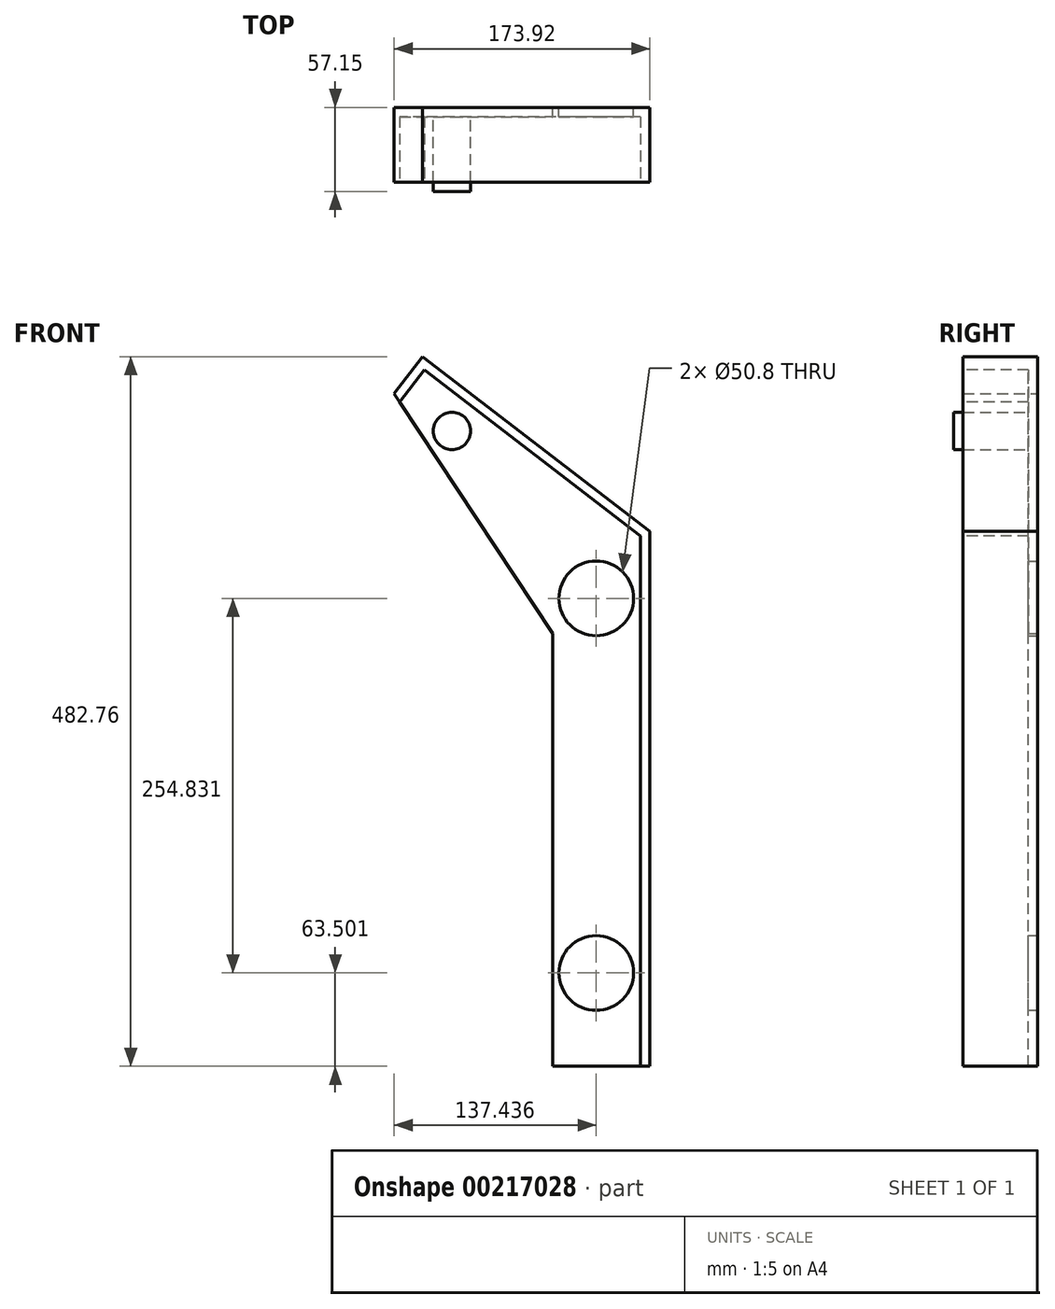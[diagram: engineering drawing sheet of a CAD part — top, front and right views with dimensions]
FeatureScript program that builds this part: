
annotation { "Feature Type Name" : "Feature", "Feature Type Description" : "" }
export const myFeature = defineFeature(function(context is Context, id is Id, definition is map)
    precondition{}
    {
        {
            var Q0;
            Q0=qCreatedBy(makeId("Front.planeOp"),FACE);
            var sketch = newSketch(context, id + "F0", { "sketchPlane" : qUnion([Q0])});
            skLineSegment(sketch, "E0.bottom", {"start": v(31, -269.09) * mm, "end": v(-35.03, -269.09) * mm});
            skLineSegment(sketch, "E0.left", {"start": v(31, -269.09) * mm, "end": v(31, 94.95) * mm});
            skLineSegment(sketch, "E0.right", {"start": v(-35.03, -269.09) * mm, "end": v(-35.03, 25.3) * mm});
            skPoint(sketch, "E0.middle", {"position": v(-5.47, 49.24) * mm});
            skLineSegment(sketch, "E1", {"start": v(31, 94.95) * mm, "end": v(-123.57, 213.67) * mm});
            skLineSegment(sketch, "E2", {"start": v(-123.57, 213.67) * mm, "end": v(-142.91, 188.5) * mm});
            skLineSegment(sketch, "E3", {"start": v(-142.91, 188.5) * mm, "end": v(-35.03, 25.3) * mm});
            skCircle(sketch, "E4", {"center": v(-5.47, 49.24) * mm, "radius": 25.4 * mm});
            skCircle(sketch, "E5", {"center": v(-5.47, -205.59) * mm, "radius": 25.4 * mm});
            skSolve(sketch);
        }
        {
            var Q0;
            Q0=makeQuery(id+"F0.imprint","IMPRINT",FACE,{"disambiguationData":[TD([[makeQuery(id+"F0.imprint","IMPRINT",EDGE,{"derivedFrom":sQuery(id+"F0.wireOp",EDGE,"E0.bottom")}),-1.0]])]});
            extrude(context, id + "F1", {"entities" : qUnion([Q0]), "depth" : 50.8 * mm});
        }
        {
            var Q0;
            Q0=makeQuery(id+"F1.opExtrude","CAP_FACE",FACE,{"disambiguationData":[OSD([sQuery(id+"F0.wireOp",EDGE,"E0.bottom"),sQuery(id+"F0.wireOp",EDGE,"E0.left"),sQuery(id+"F0.wireOp",EDGE,"E0.right"),sQuery(id+"F0.wireOp",EDGE,"E1"),sQuery(id+"F0.wireOp",EDGE,"E2"),sQuery(id+"F0.wireOp",EDGE,"E3"),sQuery(id+"F0.wireOp",EDGE,"E4"),sQuery(id+"F0.wireOp",EDGE,"E5")])],"isStart":false});
            var sketch = newSketch(context, id + "F2", { "sketchPlane" : qUnion([Q0])});
            skLineSegment(sketch, "E6.0", {"start": v(-122.4, 204.77) * mm, "end": v(-139.2, 182.89) * mm});
            skLineSegment(sketch, "E6.1", {"start": v(24.66, 91.82) * mm, "end": v(-122.4, 204.77) * mm});
            skLineSegment(sketch, "E6.2", {"start": v(24.66, -269.09) * mm, "end": v(24.66, 91.82) * mm});
            skSolve(sketch);
        }
        {
            var Q0;
            {var subQ3=sQuery(id+"F2.wireOp",EDGE,"E6.0");Q0=makeQuery(id+"F2.imprint","IMPRINT",FACE,{"disambiguationData":[TD([[makeQuery(id+"F2.imprint","IMPRINT",EDGE,{"derivedFrom":subQ3}),1.0]])]});}
            extrude(context, id + "F3", {"entities" : qUnion([Q0]), "operationType" : NewBodyOperationType.REMOVE, "oppositeDirection" : true, "depth" : 44.45 * mm});
        }
        {
            var Q0;
            Q0=makeQuery(id+"F3.boolean.opBoolean","COPY",FACE,{"derivedFrom":makeQuery(id+"F3.opExtrude","CAP_FACE",FACE,{"disambiguationData":[OSD([sQuery(id+"F0.wireOp",EDGE,"E0.bottom"),sQuery(id+"F0.wireOp",EDGE,"E0.right"),sQuery(id+"F0.wireOp",EDGE,"E3"),sQuery(id+"F0.wireOp",EDGE,"E4"),sQuery(id+"F0.wireOp",EDGE,"E5"),sQuery(id+"F2.wireOp",EDGE,"E6.0"),sQuery(id+"F2.wireOp",EDGE,"E6.1"),sQuery(id+"F2.wireOp",EDGE,"E6.2")])],"isStart":false})});
            var sketch = newSketch(context, id + "F4", { "sketchPlane" : qUnion([Q0])});
            skCircle(sketch, "E7", {"center": v(-103.57, 163.13) * mm, "radius": 12.7 * mm});
            skSolve(sketch);
        }
        {
            var Q0;
            Q0=makeQuery(id+"F4.imprint","IMPRINT",FACE,{"disambiguationData":[TD([[makeQuery(id+"F4.imprint","IMPRINT",EDGE,{"derivedFrom":sQuery(id+"F4.wireOp",EDGE,"E7")}),1.0]])]});
            extrude(context, id + "F5", {"entities" : qUnion([Q0]), "operationType" : NewBodyOperationType.ADD, "depth" : 50.8 * mm});
        }
    });
